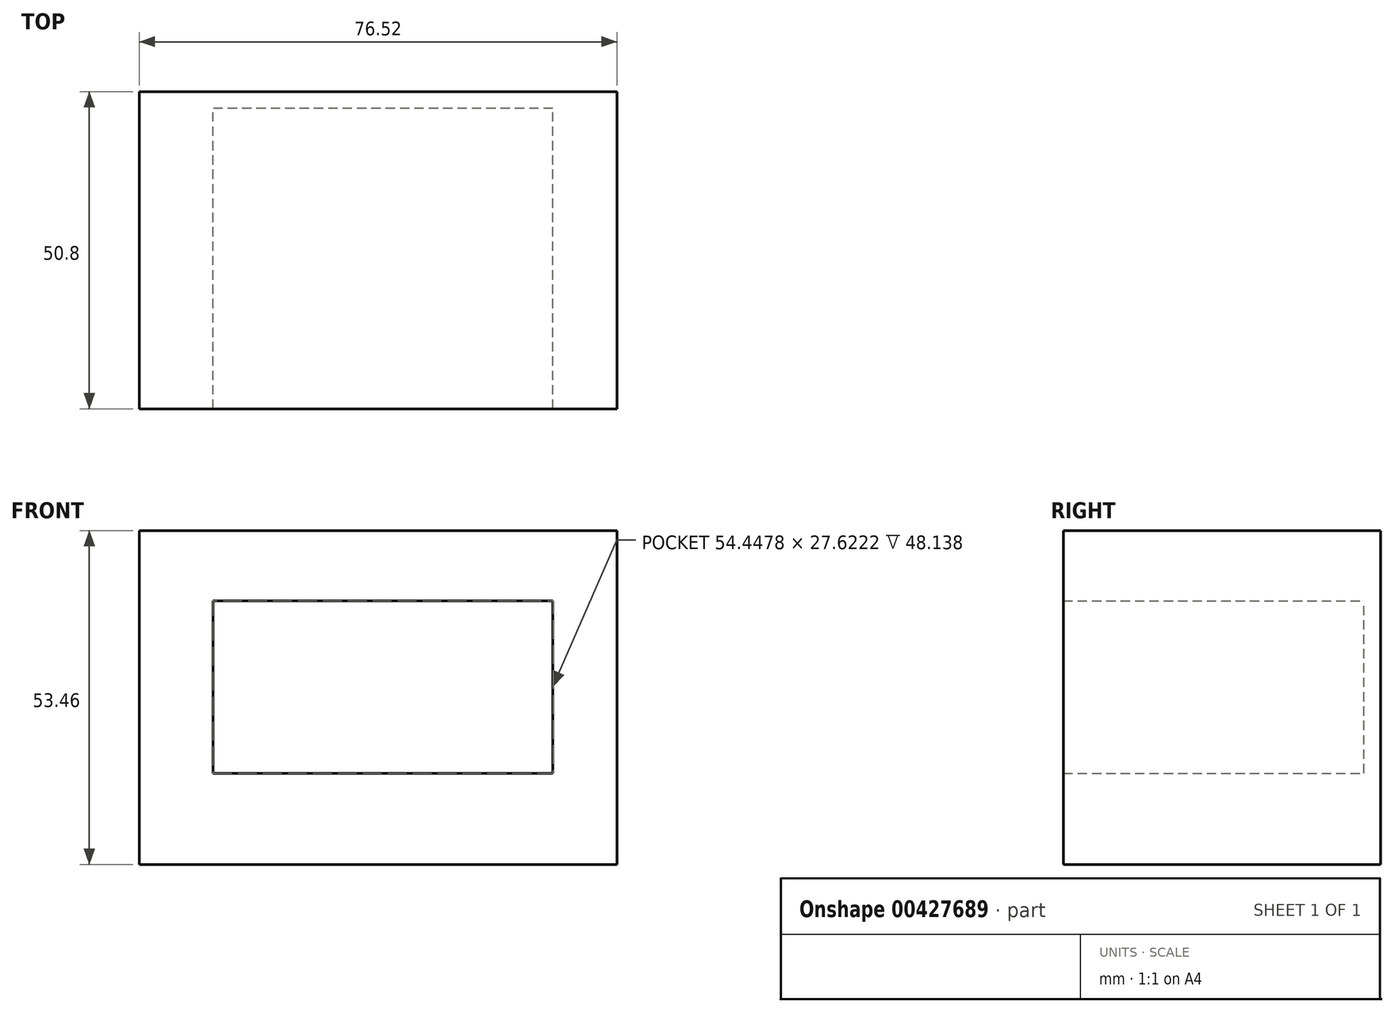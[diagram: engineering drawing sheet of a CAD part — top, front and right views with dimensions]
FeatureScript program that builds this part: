
annotation { "Feature Type Name" : "Feature", "Feature Type Description" : "" }
export const myFeature = defineFeature(function(context is Context, id is Id, definition is map)
    precondition{}
    {
        {
            var Q0;
            Q0=qCreatedBy(makeId("Front.planeOp"),FACE);
            var sketch = newSketch(context, id + "F0", { "sketchPlane" : qUnion([Q0])});
            skLineSegment(sketch, "E0.bottom", {"start": v(-26.03, 17.93) * mm, "end": v(28.42, 17.93) * mm});
            skLineSegment(sketch, "E0.top", {"start": v(-26.03, -20.58) * mm, "end": v(28.42, -20.58) * mm});
            skLineSegment(sketch, "E0.left", {"start": v(-26.03, 17.93) * mm, "end": v(-26.03, -20.58) * mm});
            skLineSegment(sketch, "E0.right", {"start": v(28.42, 17.93) * mm, "end": v(28.42, -20.58) * mm});
            skLineSegment(sketch, "E1", {"start": v(-26.03, 12.62) * mm, "end": v(28.42, 12.62) * mm});
            skLineSegment(sketch, "E2", {"start": v(-26.03, -15) * mm, "end": v(28.42, -15) * mm});
            skLineSegment(sketch, "E3.bottom", {"start": v(38.67, 23.85) * mm, "end": v(-37.85, 23.85) * mm});
            skLineSegment(sketch, "E3.top", {"start": v(38.67, -29.61) * mm, "end": v(-37.85, -29.61) * mm});
            skLineSegment(sketch, "E3.left", {"start": v(38.67, 23.85) * mm, "end": v(38.67, -29.61) * mm});
            skLineSegment(sketch, "E3.right", {"start": v(-37.85, 23.85) * mm, "end": v(-37.85, -29.61) * mm});
            skSolve(sketch);
        }
        {
            var Q0;
            {var subQ6=sQuery(id+"F0.wireOp",EDGE,"E0.bottom");Q0=makeQuery(id+"F0.imprint","IMPRINT",FACE,{"disambiguationData":[TD([[makeQuery(id+"F0.imprint","IMPRINT",EDGE,{"derivedFrom":subQ6}),1.0]])]});}
            var Q1;
            {var subQ0=sQuery(id+"F0.wireOp",EDGE,"E0.bottom");Q1=makeQuery(id+"F0.imprint","IMPRINT",FACE,{"disambiguationData":[TD([[makeQuery(id+"F0.imprint","IMPRINT",EDGE,{"derivedFrom":subQ0}),-1.0]])]});}
            var Q2;
            {var subQ0=sQuery(id+"F0.wireOp",EDGE,"E0.top");Q2=makeQuery(id+"F0.imprint","IMPRINT",FACE,{"disambiguationData":[TD([[makeQuery(id+"F0.imprint","IMPRINT",EDGE,{"derivedFrom":subQ0}),1.0]])]});}
            extrude(context, id + "F1", {"entities" : qUnion([Q0, Q1, Q2]), "depth" : 50.8 * mm});
        }
        {
            var Q0;
            Q0=makeQuery(id+"F1.opExtrude","SWEPT_FACE",FACE,{"disambiguationData":[OSD([sQuery(id+"F0.wireOp",EDGE,"E1")])]});
            var sketch = newSketch(context, id + "F2", { "sketchPlane" : qUnion([Q0])});
            skLineSegment(sketch, "E4.bottom", {"start": v(28.42, 0) * mm, "end": v(-26.03, 0) * mm});
            skLineSegment(sketch, "E4.top", {"start": v(28.42, 2.66) * mm, "end": v(-26.03, 2.66) * mm});
            skLineSegment(sketch, "E4.left", {"start": v(28.42, 0) * mm, "end": v(28.42, 2.66) * mm});
            skLineSegment(sketch, "E4.right", {"start": v(-26.03, 0) * mm, "end": v(-26.03, 2.66) * mm});
            skSolve(sketch);
        }
        {
            var Q0;
            Q0 = qSketchRegion(id + "F2", true);
            extrude(context, id + "F3", {"entities" : qUnion([Q0]), "operationType" : NewBodyOperationType.ADD, "depth" : 30.6 * mm});
        }
    });
